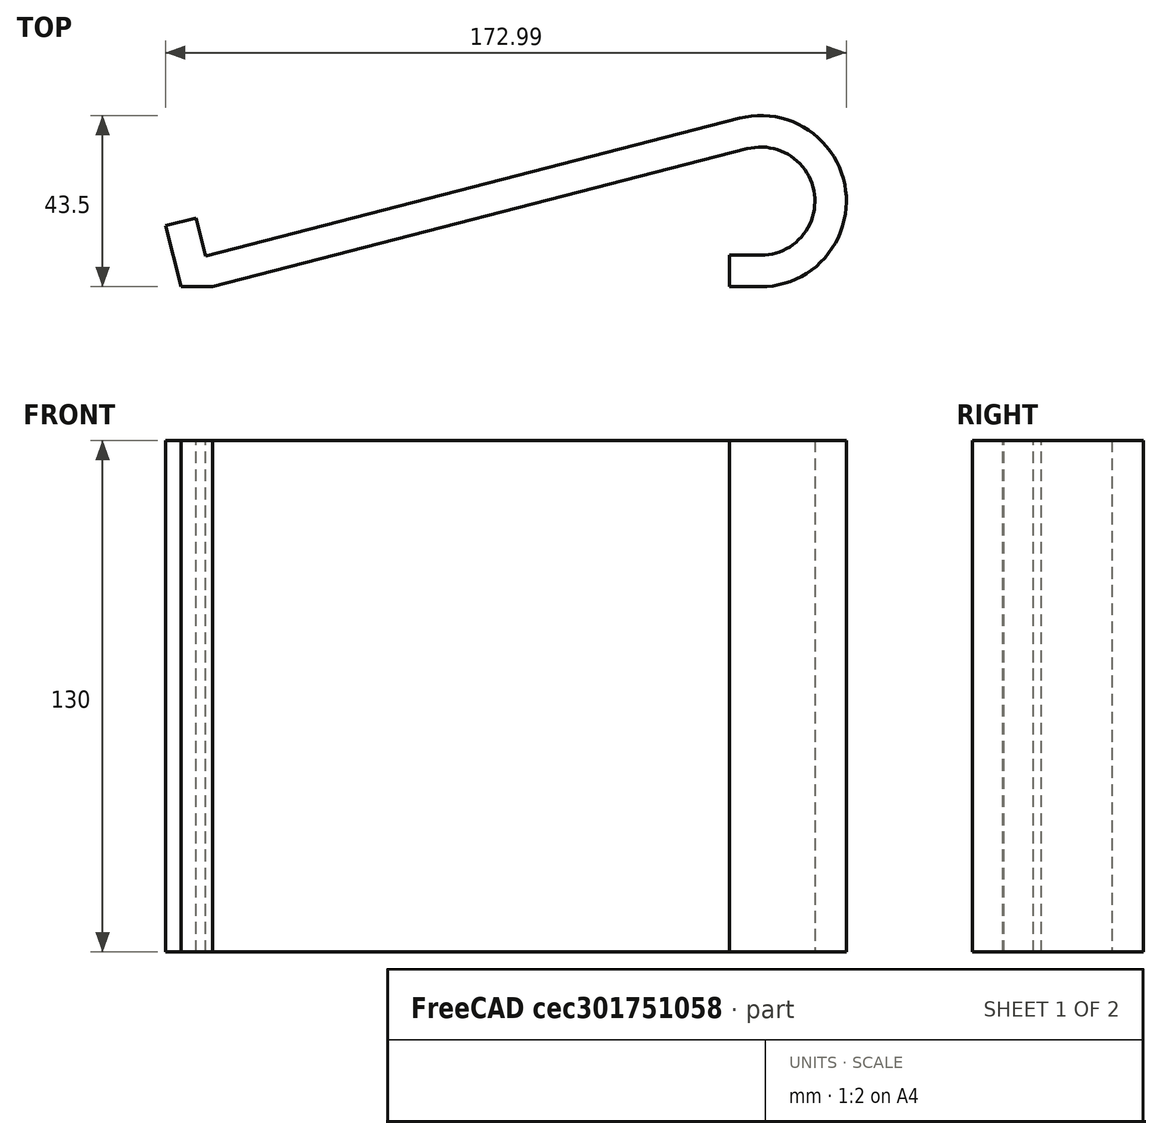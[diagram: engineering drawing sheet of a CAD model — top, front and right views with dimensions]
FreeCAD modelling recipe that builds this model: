
FCSTD DOCUMENT  (FreeCAD 0.19R24291 (Git))
Label: speakerstand
License: All rights reserved
LicenseURL: http://en.wikipedia.org/wiki/All_rights_reserved
objects: Sketcher::SketchObject×1, PartDesign::Pad×1, PartDesign::Body×1, Spreadsheet::Sheet×1
note: 4 computed .brp shape members not serialized (recipe doc carries the construction recipe); baked Part::Feature solids carry a one-line shape summary decoded from their .brp

FEATURE [Sketcher::SketchObject] Sketch
  FullyConstrained = true
  MapMode = 5
  Support = -> [XY_Plane]
  expr: Constraints[22] = Spreadsheet.Thickness
  expr: Constraints[41] = Spreadsheet.Slope
  expr: Constraints[39] = Spreadsheet.Depth
  sketch-geometry (20):
    g0: LineSegment StartX=0 StartY=0 StartZ=0 EndX=8 EndY=0 EndZ=0
    g1: LineSegment StartX=8 StartY=0 StartZ=0 EndX=143.8 EndY=35.0635 EndZ=0
    g2: LineSegment StartX=0 StartY=0 StartZ=0 EndX=-4 EndY=15.4919 EndZ=0
    g3: LineSegment StartX=-4 StartY=15.4919 StartZ=0 EndX=3.74597 EndY=17.4919 EndZ=0
    g4: LineSegment StartX=3.74597 StartY=17.4919 StartZ=0 EndX=6.24597 EndY=7.80948 EndZ=0
    g5: LineSegment StartX=6.24597 StartY=7.80948 StartZ=0 EndX=141.8 EndY=42.8095 EndZ=0
    g6: LineSegment StartX=139.238 StartY=8 StartZ=0 EndX=139.238 EndY=0 EndZ=0
    g7: LineSegment StartX=139.238 StartY=0 StartZ=0 EndX=147.238 EndY=2.451e-13 EndZ=0
    g8: LineSegment StartX=139.238 StartY=8 StartZ=0 EndX=147.238 EndY=8 EndZ=0
    g9: ArcOfCircle CenterX=147.238 CenterY=21.7501 CenterZ=0 NormalX=0 NormalY=0 NormalZ=1 AngleXU=0 Radius=13.7501 StartAngle=4.71239 EndAngle=8.10666
    g10: ArcOfCircle CenterX=147.238 CenterY=21.7501 CenterZ=0 NormalX=0 NormalY=0 NormalZ=1 AngleXU=0 Radius=21.7501 StartAngle=4.71239 EndAngle=8.10666
    g11: GeomPoint X=147.238 Y=8 Z=0
    g12: GeomPoint X=147.238 Y=8 Z=0
    g13: GeomPoint X=147.238 Y=8 Z=0
    g14: GeomPoint X=147.238 Y=8 Z=0
    g15: GeomPoint X=147.238 Y=2.451e-13 Z=0
    g16: GeomPoint X=147.238 Y=2.451e-13 Z=0
    g17: GeomPoint X=147.238 Y=2.451e-13 Z=0
    g18: GeomPoint X=147.238 Y=2.451e-13 Z=0
    g19: LineSegment StartX=141.8 StartY=42.8095 StartZ=0 EndX=143.8 EndY=35.0635 EndZ=0
  constraints (43):
    c: Coincident(g0,g-1)
    c: PointOnObject(g0,g-1)
    c: Coincident(g1,g0)
    c: Coincident(g2,g0)
    c: Coincident(g3,g2)
    c: Coincident(g4,g3)
    c: Coincident(g5,g4)
    c: PointOnObject(g6,g-1)
    c: Vertical(g6)
    c: Coincident(g7,g6)
    c: PointOnObject(g7,g-1)
    c: Coincident(g8,g6)
    c: Horizontal(g8)
    c: Coincident(g9,g1)
    c: Coincident(g10,g9)
    c: Coincident(g10,g5)
    c: Coincident(g11,g9)
    c: Coincident(g12,g8)
    c: Coincident(g13,g9)
    c: Coincident(g14,g8)
    c: Coincident(g15,g10)
    c: Coincident(g16,g7)
    c: DistanceY(g6,g6) = 8
    c: Coincident(g17,g10)
    c: Coincident(g18,g7)
    c: Perpendicular(g5,g4)
    c: Perpendicular(g3,g4)
    c: Perpendicular(g2,g3)
    c: Coincident(g19,g5)
    c: Coincident(g19,g1)
    c: Equal(g3,g19)
    c: Perpendicular(g5,g19)
    c: Tangent(g10,g5)
    c: Equal(g19,g6)
    c: Parallel(g1,g5)
    c: Coincident(g8,g9)
    c: Coincident(g7,g10)
    c: Tangent(g8,g9)
    c: Equal(g6,g7)
    c: Distance(g5) = 140
    c: Distance(g4) = 10
    c: DistanceY(g4,g5) = 35
    c: Equal(g3,g0)
FEATURE [PartDesign::Pad] Pad
  Direction = (1,1,1)
  Length = 130
  Length2 = 100
  Profile = -> Sketch
  Type = 0
  expr: Length = Spreadsheet.Width
FEATURE [PartDesign::Body] Body
  Group = -> [Sketch,Pad]
  Origin = -> Origin
  Tip = -> Pad
FEATURE [Spreadsheet::Sheet] Spreadsheet
  cells = A2=Depth; B2(Depth)=140; A3=Width; B3(Width)=130; A4=Slope; B4(Slope)=35; A5=Thickness; B5(Thickness)=8
